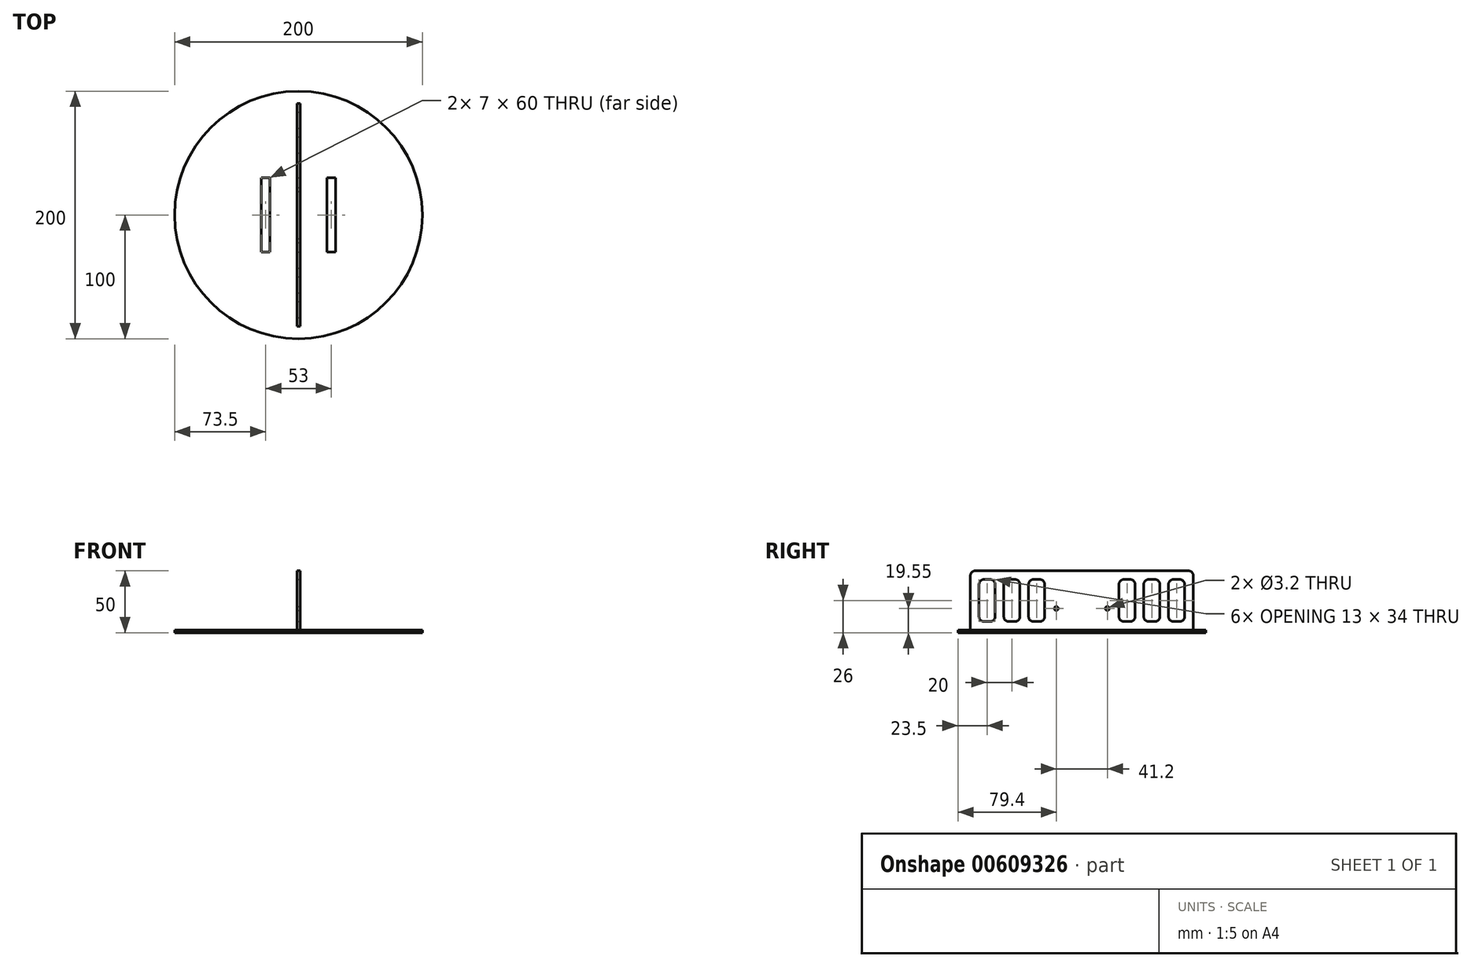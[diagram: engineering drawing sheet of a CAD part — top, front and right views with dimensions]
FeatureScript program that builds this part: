
annotation { "Feature Type Name" : "Feature", "Feature Type Description" : "" }
export const myFeature = defineFeature(function(context is Context, id is Id, definition is map)
    precondition{}
    {
        {
            var Q0;
            Q0=qCreatedBy(makeId("Top.planeOp"),FACE);
            var sketch = newSketch(context, id + "F0", { "sketchPlane" : qUnion([Q0])});
            skCircle(sketch, "E0", {"center": v(0, 0) * mm, "radius": 100 * mm});
            skLineSegment(sketch, "E1.bottom", {"start": v(-23, 30) * mm, "end": v(-30, 30) * mm});
            skLineSegment(sketch, "E1.top", {"start": v(-23, -30) * mm, "end": v(-30, -30) * mm});
            skLineSegment(sketch, "E1.left", {"start": v(-23, 30) * mm, "end": v(-23, -30) * mm});
            skLineSegment(sketch, "E1.right", {"start": v(-30, 30) * mm, "end": v(-30, -30) * mm});
            skPoint(sketch, "E1.middle", {"position": v(-26.5, 0) * mm});
            skLineSegment(sketch, "E2.MirrorCS", {"start": v(23, 30) * mm, "end": v(30, 30) * mm});
            skLineSegment(sketch, "E3.MirrorCS", {"start": v(23, 30) * mm, "end": v(23, -30) * mm});
            skLineSegment(sketch, "E4.MirrorCS", {"start": v(23, -30) * mm, "end": v(30, -30) * mm});
            skLineSegment(sketch, "E5.MirrorCS", {"start": v(30, 30) * mm, "end": v(30, -30) * mm});
            skPoint(sketch, "E6.MirrorP", {"position": v(26.5, 0) * mm});
            skLineSegment(sketch, "E7.bottom", {"start": v(1.25, 90) * mm, "end": v(-1.25, 90) * mm});
            skLineSegment(sketch, "E7.top", {"start": v(1.25, -90) * mm, "end": v(-1.25, -90) * mm});
            skLineSegment(sketch, "E7.left", {"start": v(1.25, 90) * mm, "end": v(1.25, -90) * mm});
            skLineSegment(sketch, "E7.right", {"start": v(-1.25, 90) * mm, "end": v(-1.25, -90) * mm});
            skSolve(sketch);
        }
        {
            var Q0;
            Q0 = qSketchRegion(id + "F0", true);
            extrude(context, id + "F1", {"entities" : qUnion([Q0]), "depth" : 2 * mm, "offsetDistance" : 25.4 * mm});
        }
        {
            var Q0;
            Q0=makeQuery(id+"F0.imprint","IMPRINT",FACE,{"disambiguationData":[TD([[makeQuery(id+"F0.imprint","IMPRINT",EDGE,{"derivedFrom":sQuery(id+"F0.wireOp",EDGE,"E7.bottom")}),1.0]])]});
            extrude(context, id + "F2", {"entities" : qUnion([Q0]), "operationType" : NewBodyOperationType.ADD, "depth" : 50 * mm, "offsetDistance" : 25.4 * mm});
        }
        {
            var Q0;
            Q0=makeQuery(id+"F2.opExtrude","SWEPT_FACE",FACE,{"disambiguationData":[OSD([sQuery(id+"F0.wireOp",EDGE,"E7.left")])]});
            var sketch = newSketch(context, id + "F3", { "sketchPlane" : qUnion([Q0])});
            skCircle(sketch, "E8", {"center": v(-20.6, 19.55) * mm, "radius": 1.6 * mm});
            skCircle(sketch, "E9.MirrorC", {"center": v(20.6, 19.55) * mm, "radius": 1.6 * mm});
            skLineSegment(sketch, "E10.bottom", {"start": v(-83, 43) * mm, "end": v(-70, 43) * mm});
            skLineSegment(sketch, "E10.top", {"start": v(-83, 9) * mm, "end": v(-70, 9) * mm});
            skLineSegment(sketch, "E10.left", {"start": v(-83, 43) * mm, "end": v(-83, 9) * mm});
            skLineSegment(sketch, "E10.right", {"start": v(-70, 43) * mm, "end": v(-70, 9) * mm});
            skLineSegment(sketch, "E11.1.0.0", {"start": v(-63, 43) * mm, "end": v(-63, 9) * mm});
            skLineSegment(sketch, "E11.1.0.1", {"start": v(-63, 9) * mm, "end": v(-50, 9) * mm});
            skLineSegment(sketch, "E11.1.0.2", {"start": v(-50, 43) * mm, "end": v(-50, 9) * mm});
            skLineSegment(sketch, "E11.1.0.3", {"start": v(-63, 43) * mm, "end": v(-50, 43) * mm});
            skLineSegment(sketch, "E11.2.0.0", {"start": v(-43, 43) * mm, "end": v(-43, 9) * mm});
            skLineSegment(sketch, "E11.2.0.1", {"start": v(-43, 9) * mm, "end": v(-30, 9) * mm});
            skLineSegment(sketch, "E11.2.0.2", {"start": v(-30, 43) * mm, "end": v(-30, 9) * mm});
            skLineSegment(sketch, "E11.2.0.3", {"start": v(-43, 43) * mm, "end": v(-30, 43) * mm});
            skLineSegment(sketch, "E11.direction1", {"start": v(-83, 9) * mm, "end": v(-63, 9) * mm, "construction": true});
            skLineSegment(sketch, "E12.MirrorCS", {"start": v(83, 9) * mm, "end": v(70, 9) * mm});
            skLineSegment(sketch, "E13.MirrorCS", {"start": v(63, 43) * mm, "end": v(63, 9) * mm});
            skLineSegment(sketch, "E14.MirrorCS", {"start": v(43, 43) * mm, "end": v(43, 9) * mm});
            skLineSegment(sketch, "E15.MirrorCS", {"start": v(70, 43) * mm, "end": v(70, 9) * mm});
            skLineSegment(sketch, "E16.MirrorCS", {"start": v(63, 9) * mm, "end": v(50, 9) * mm});
            skLineSegment(sketch, "E17.MirrorCS", {"start": v(43, 9) * mm, "end": v(30, 9) * mm});
            skLineSegment(sketch, "E18.MirrorCS", {"start": v(83, 43) * mm, "end": v(70, 43) * mm});
            skLineSegment(sketch, "E19.MirrorCS", {"start": v(43, 43) * mm, "end": v(30, 43) * mm});
            skLineSegment(sketch, "E20.MirrorCS", {"start": v(30, 43) * mm, "end": v(30, 9) * mm});
            skLineSegment(sketch, "E21.MirrorCS", {"start": v(50, 43) * mm, "end": v(50, 9) * mm});
            skLineSegment(sketch, "E22.MirrorCS", {"start": v(63, 43) * mm, "end": v(50, 43) * mm});
            skLineSegment(sketch, "E23.MirrorCS", {"start": v(83, 9) * mm, "end": v(63, 9) * mm, "construction": true});
            skLineSegment(sketch, "E24.MirrorCS", {"start": v(83, 43) * mm, "end": v(83, 9) * mm});
            skSolve(sketch);
        }
        {
            var Q0;
            Q0 = qSketchRegion(id + "F3", true);
            extrude(context, id + "F4", {"entities" : qUnion([Q0]), "operationType" : NewBodyOperationType.REMOVE, "oppositeDirection" : true, "depth" : 4 * mm, "offsetDistance" : 25.4 * mm});
        }
        {
            var Q0;
            Q0=makeQuery(id+"F2.opExtrude","CAP_EDGE",EDGE,{"disambiguationData":[OSD([sQuery(id+"F0.wireOp",EDGE,"E7.top")])],"isStart":false});
            var Q1;
            Q1=makeQuery(id+"F2.opExtrude","CAP_EDGE",EDGE,{"disambiguationData":[OSD([sQuery(id+"F0.wireOp",EDGE,"E7.bottom")])],"isStart":false});
            var Q2;
            Q2=makeQuery(id+"F4.boolean.opBoolean","COPY",EDGE,{"derivedFrom":makeQuery(id+"F4.opExtrude","SWEPT_EDGE",EDGE,{"disambiguationData":[OSD([sQuery(id+"F3.wireOp",EDGE,"E16.MirrorCS"),sQuery(id+"F3.wireOp",EDGE,"E21.MirrorCS")])]})});
            var Q3;
            Q3=makeQuery(id+"F4.boolean.opBoolean","COPY",EDGE,{"derivedFrom":makeQuery(id+"F4.opExtrude","SWEPT_EDGE",EDGE,{"disambiguationData":[OSD([sQuery(id+"F3.wireOp",EDGE,"E13.MirrorCS"),sQuery(id+"F3.wireOp",EDGE,"E16.MirrorCS")])]})});
            var Q4;
            Q4=makeQuery(id+"F4.boolean.opBoolean","COPY",EDGE,{"derivedFrom":makeQuery(id+"F4.opExtrude","SWEPT_EDGE",EDGE,{"disambiguationData":[OSD([sQuery(id+"F3.wireOp",EDGE,"E12.MirrorCS"),sQuery(id+"F3.wireOp",EDGE,"E24.MirrorCS")])]})});
            var Q5;
            Q5=makeQuery(id+"F4.boolean.opBoolean","COPY",EDGE,{"derivedFrom":makeQuery(id+"F4.opExtrude","SWEPT_EDGE",EDGE,{"disambiguationData":[OSD([sQuery(id+"F3.wireOp",EDGE,"E12.MirrorCS"),sQuery(id+"F3.wireOp",EDGE,"E15.MirrorCS")])]})});
            var Q6;
            Q6=makeQuery(id+"F4.boolean.opBoolean","COPY",EDGE,{"derivedFrom":makeQuery(id+"F4.opExtrude","SWEPT_EDGE",EDGE,{"disambiguationData":[OSD([sQuery(id+"F3.wireOp",EDGE,"E17.MirrorCS"),sQuery(id+"F3.wireOp",EDGE,"E20.MirrorCS")])]})});
            var Q7;
            Q7=makeQuery(id+"F4.boolean.opBoolean","COPY",EDGE,{"derivedFrom":makeQuery(id+"F4.opExtrude","SWEPT_EDGE",EDGE,{"disambiguationData":[OSD([sQuery(id+"F3.wireOp",EDGE,"E11.2.0.0"),sQuery(id+"F3.wireOp",EDGE,"E11.2.0.1")])]})});
            var Q8;
            Q8=makeQuery(id+"F4.boolean.opBoolean","COPY",EDGE,{"derivedFrom":makeQuery(id+"F4.opExtrude","SWEPT_EDGE",EDGE,{"disambiguationData":[OSD([sQuery(id+"F3.wireOp",EDGE,"E18.MirrorCS"),sQuery(id+"F3.wireOp",EDGE,"E24.MirrorCS")])]})});
            var Q9;
            Q9=makeQuery(id+"F4.boolean.opBoolean","COPY",EDGE,{"derivedFrom":makeQuery(id+"F4.opExtrude","SWEPT_EDGE",EDGE,{"disambiguationData":[OSD([sQuery(id+"F3.wireOp",EDGE,"E13.MirrorCS"),sQuery(id+"F3.wireOp",EDGE,"E22.MirrorCS")])]})});
            var Q10;
            Q10=makeQuery(id+"F4.boolean.opBoolean","COPY",EDGE,{"derivedFrom":makeQuery(id+"F4.opExtrude","SWEPT_EDGE",EDGE,{"disambiguationData":[OSD([sQuery(id+"F3.wireOp",EDGE,"E14.MirrorCS"),sQuery(id+"F3.wireOp",EDGE,"E19.MirrorCS")])]})});
            var Q11;
            Q11=makeQuery(id+"F4.boolean.opBoolean","COPY",EDGE,{"derivedFrom":makeQuery(id+"F4.opExtrude","SWEPT_EDGE",EDGE,{"disambiguationData":[OSD([sQuery(id+"F3.wireOp",EDGE,"E11.2.0.2"),sQuery(id+"F3.wireOp",EDGE,"E11.2.0.3")])]})});
            var Q12;
            Q12=makeQuery(id+"F4.boolean.opBoolean","COPY",EDGE,{"derivedFrom":makeQuery(id+"F4.opExtrude","SWEPT_EDGE",EDGE,{"disambiguationData":[OSD([sQuery(id+"F3.wireOp",EDGE,"E11.1.0.2"),sQuery(id+"F3.wireOp",EDGE,"E11.1.0.3")])]})});
            var Q13;
            Q13=makeQuery(id+"F4.boolean.opBoolean","COPY",EDGE,{"derivedFrom":makeQuery(id+"F4.opExtrude","SWEPT_EDGE",EDGE,{"disambiguationData":[OSD([sQuery(id+"F3.wireOp",EDGE,"E10.bottom"),sQuery(id+"F3.wireOp",EDGE,"E10.right")])]})});
            var Q14;
            Q14=makeQuery(id+"F4.boolean.opBoolean","COPY",EDGE,{"derivedFrom":makeQuery(id+"F4.opExtrude","SWEPT_EDGE",EDGE,{"disambiguationData":[OSD([sQuery(id+"F3.wireOp",EDGE,"E10.top"),sQuery(id+"F3.wireOp",EDGE,"E10.right")])]})});
            var Q15;
            Q15=makeQuery(id+"F4.boolean.opBoolean","COPY",EDGE,{"derivedFrom":makeQuery(id+"F4.opExtrude","SWEPT_EDGE",EDGE,{"disambiguationData":[OSD([sQuery(id+"F3.wireOp",EDGE,"E11.1.0.1"),sQuery(id+"F3.wireOp",EDGE,"E11.1.0.2")])]})});
            var Q16;
            Q16=makeQuery(id+"F4.boolean.opBoolean","COPY",EDGE,{"derivedFrom":makeQuery(id+"F4.opExtrude","SWEPT_EDGE",EDGE,{"disambiguationData":[OSD([sQuery(id+"F3.wireOp",EDGE,"E11.2.0.1"),sQuery(id+"F3.wireOp",EDGE,"E11.2.0.2")])]})});
            var Q17;
            Q17=makeQuery(id+"F4.boolean.opBoolean","COPY",EDGE,{"derivedFrom":makeQuery(id+"F4.opExtrude","SWEPT_EDGE",EDGE,{"disambiguationData":[OSD([sQuery(id+"F3.wireOp",EDGE,"E11.1.0.0"),sQuery(id+"F3.wireOp",EDGE,"E11.1.0.1")])]})});
            var Q18;
            Q18=makeQuery(id+"F4.boolean.opBoolean","COPY",EDGE,{"derivedFrom":makeQuery(id+"F4.opExtrude","SWEPT_EDGE",EDGE,{"disambiguationData":[OSD([sQuery(id+"F3.wireOp",EDGE,"E10.top"),sQuery(id+"F3.wireOp",EDGE,"E10.left")])]})});
            var Q19;
            Q19=makeQuery(id+"F4.boolean.opBoolean","COPY",EDGE,{"derivedFrom":makeQuery(id+"F4.opExtrude","SWEPT_EDGE",EDGE,{"disambiguationData":[OSD([sQuery(id+"F3.wireOp",EDGE,"E15.MirrorCS"),sQuery(id+"F3.wireOp",EDGE,"E18.MirrorCS")])]})});
            var Q20;
            Q20=makeQuery(id+"F4.boolean.opBoolean","COPY",EDGE,{"derivedFrom":makeQuery(id+"F4.opExtrude","SWEPT_EDGE",EDGE,{"disambiguationData":[OSD([sQuery(id+"F3.wireOp",EDGE,"E21.MirrorCS"),sQuery(id+"F3.wireOp",EDGE,"E22.MirrorCS")])]})});
            var Q21;
            Q21=makeQuery(id+"F4.boolean.opBoolean","COPY",EDGE,{"derivedFrom":makeQuery(id+"F4.opExtrude","SWEPT_EDGE",EDGE,{"disambiguationData":[OSD([sQuery(id+"F3.wireOp",EDGE,"E19.MirrorCS"),sQuery(id+"F3.wireOp",EDGE,"E20.MirrorCS")])]})});
            var Q22;
            Q22=makeQuery(id+"F4.boolean.opBoolean","COPY",EDGE,{"derivedFrom":makeQuery(id+"F4.opExtrude","SWEPT_EDGE",EDGE,{"disambiguationData":[OSD([sQuery(id+"F3.wireOp",EDGE,"E11.1.0.0"),sQuery(id+"F3.wireOp",EDGE,"E11.1.0.3")])]})});
            var Q23;
            Q23=makeQuery(id+"F4.boolean.opBoolean","COPY",EDGE,{"derivedFrom":makeQuery(id+"F4.opExtrude","SWEPT_EDGE",EDGE,{"disambiguationData":[OSD([sQuery(id+"F3.wireOp",EDGE,"E11.2.0.0"),sQuery(id+"F3.wireOp",EDGE,"E11.2.0.3")])]})});
            var Q24;
            Q24=makeQuery(id+"F4.boolean.opBoolean","COPY",EDGE,{"derivedFrom":makeQuery(id+"F4.opExtrude","SWEPT_EDGE",EDGE,{"disambiguationData":[OSD([sQuery(id+"F3.wireOp",EDGE,"E10.bottom"),sQuery(id+"F3.wireOp",EDGE,"E10.left")])]})});
            var Q25;
            Q25=makeQuery(id+"F4.boolean.opBoolean","COPY",EDGE,{"derivedFrom":makeQuery(id+"F4.opExtrude","SWEPT_EDGE",EDGE,{"disambiguationData":[OSD([sQuery(id+"F3.wireOp",EDGE,"E14.MirrorCS"),sQuery(id+"F3.wireOp",EDGE,"E17.MirrorCS")])]})});
            fillet(context, id + "F5", {"entities" : qUnion([Q0, Q1, Q2, Q3, Q4, Q5, Q6, Q7, Q8, Q9, Q10, Q11, Q12, Q13, Q14, Q15, Q16, Q17, Q18, Q19, Q20, Q21, Q22, Q23, Q24, Q25]), "radius" : 4 * mm, "tangentPropagation" : true, "allowEdgeOverflow" : false});
        }
    });
